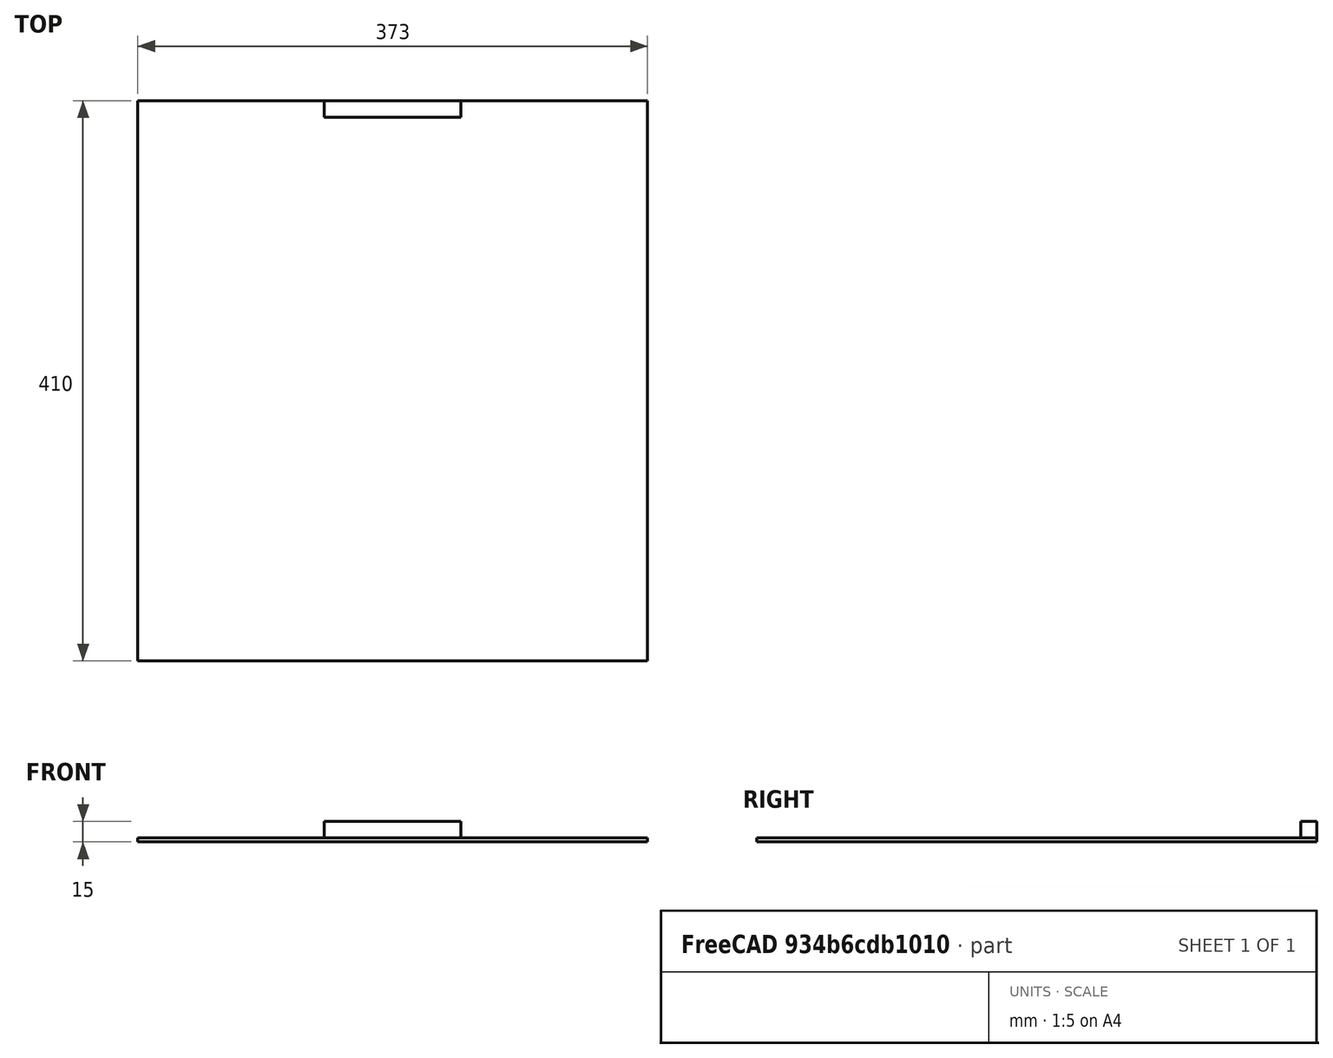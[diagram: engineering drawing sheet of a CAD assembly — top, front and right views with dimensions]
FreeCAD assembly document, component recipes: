
FREECAD ASSEMBLY — COMPONENT RECIPES ("testna_plosca")

This assembly document has 2 components, labeled P0..P1 below (a component is one placed body or linked part). 2 of them carry a construction recipe — the FreeCAD feature program that regenerates the part from scratch, quoted from this document or its linked companion documents; the rest are supplied as boundary geometry only. No exploded tour is included for this assembly.
COMPONENT P0 — recipe-attached ("handle", modeled in this document).
Construction recipe (the document's own serialized feature program — sketch geometry with constraints, then the solid features built on it; lengths are millimeters unless a unit is written):

FEATURE [PartDesign::CoordinateSystem] LCS_0003
  AttacherType = Attacher::AttachEngine3D
  MapMode = 2
  Support = -> [X_Axis004]
FEATURE [Sketcher::SketchObject] Sketch001
  FullyConstrained = true
  MapMode = 5
  Placement = pos=(0,0,0) rot=(0.57735,0.57735,0.57735;2.0944rad)
  Support = -> [YZ_Plane004]
  expr: Constraints[8] = Variables.depth
  sketch-geometry (4):
    g0: LineSegment StartX=398 StartY=15 StartZ=0 EndX=410 EndY=15 EndZ=0
    g1: LineSegment StartX=410 StartY=15 StartZ=0 EndX=410 EndY=3 EndZ=0
    g2: LineSegment StartX=410 StartY=3 StartZ=0 EndX=398 EndY=3 EndZ=0
    g3: LineSegment StartX=398 StartY=3 StartZ=0 EndX=398 EndY=15 EndZ=0
  constraints (12):
    c: Coincident(g0,g1)
    c: Coincident(g1,g2)
    c: Coincident(g2,g3)
    c: Coincident(g3,g0)
    c: Horizontal(g0)
    c: Horizontal(g2)
    c: Vertical(g1)
    c: Vertical(g3)
    c: DistanceX(g-1,g1) = 410
    c: DistanceY(g-1,g1) = 3
    c: DistanceY(g1,g1) = 12
    c: DistanceX(g0,g0) = 12
FEATURE [PartDesign::Pad] Pad001
  Direction = (1,1,1)
  Length = 100
  Length2 = 100
  Midplane = true
  Placement = pos=(0,0,0) rot=(0.57735,0.57735,0.57735;2.0944rad)
  Profile = -> Sketch001
  Type = 0
FEATURE [PartDesign::Body] Body_2
  Group = -> [LCS_0003,Sketch001,Pad001]
  Origin = -> Origin004
  Tip = -> Pad001
COMPONENT P1 — recipe-attached ("plate", modeled in this document).
Construction recipe (the document's own serialized feature program — sketch geometry with constraints, then the solid features built on it; lengths are millimeters unless a unit is written):

FEATURE [PartDesign::CoordinateSystem] LCS_0001
  AttacherType = Attacher::AttachEngine3D
  MapMode = 2
  Support = -> [X_Axis002]
FEATURE [Sketcher::SketchObject] Sketch
  FullyConstrained = true
  MapMode = 5
  Support = -> [XY_Plane002]
  expr: Constraints[9] = Variables.width
  expr: Constraints[10] = Variables.depth
  sketch-geometry (4):
    g0: LineSegment StartX=-186.5 StartY=0 StartZ=0 EndX=186.5 EndY=0 EndZ=0
    g1: LineSegment StartX=186.5 StartY=0 StartZ=0 EndX=186.5 EndY=410 EndZ=0
    g2: LineSegment StartX=186.5 StartY=410 StartZ=0 EndX=-186.5 EndY=410 EndZ=0
    g3: LineSegment StartX=-186.5 StartY=410 StartZ=0 EndX=-186.5 EndY=0 EndZ=0
  constraints (11):
    c: Coincident(g0,g1)
    c: Coincident(g1,g2)
    c: Coincident(g2,g3)
    c: Coincident(g3,g0)
    c: Horizontal(g0)
    c: Horizontal(g2)
    c: Vertical(g1)
    c: Vertical(g3)
    c: Symmetric(g0,g0,g-1)
    c: DistanceX(g0,g0) = 373
    c: DistanceY(g1,g1) = 410
FEATURE [PartDesign::Pad] Pad
  Direction = (1,1,1)
  Length = 3
  Length2 = 100
  Profile = -> Sketch
  Type = 0
FEATURE [PartDesign::Body] Body
  Group = -> [LCS_0001,Sketch,Pad]
  Origin = -> Origin002
  Tip = -> Pad
PROVENANCE & LICENSES
A FreeCAD (.FCStd) document from a public repository crawl; recipes are the document's own serialized feature recipes (and, for linked parts, companion documents' recipes).
License: apache-2.0.
